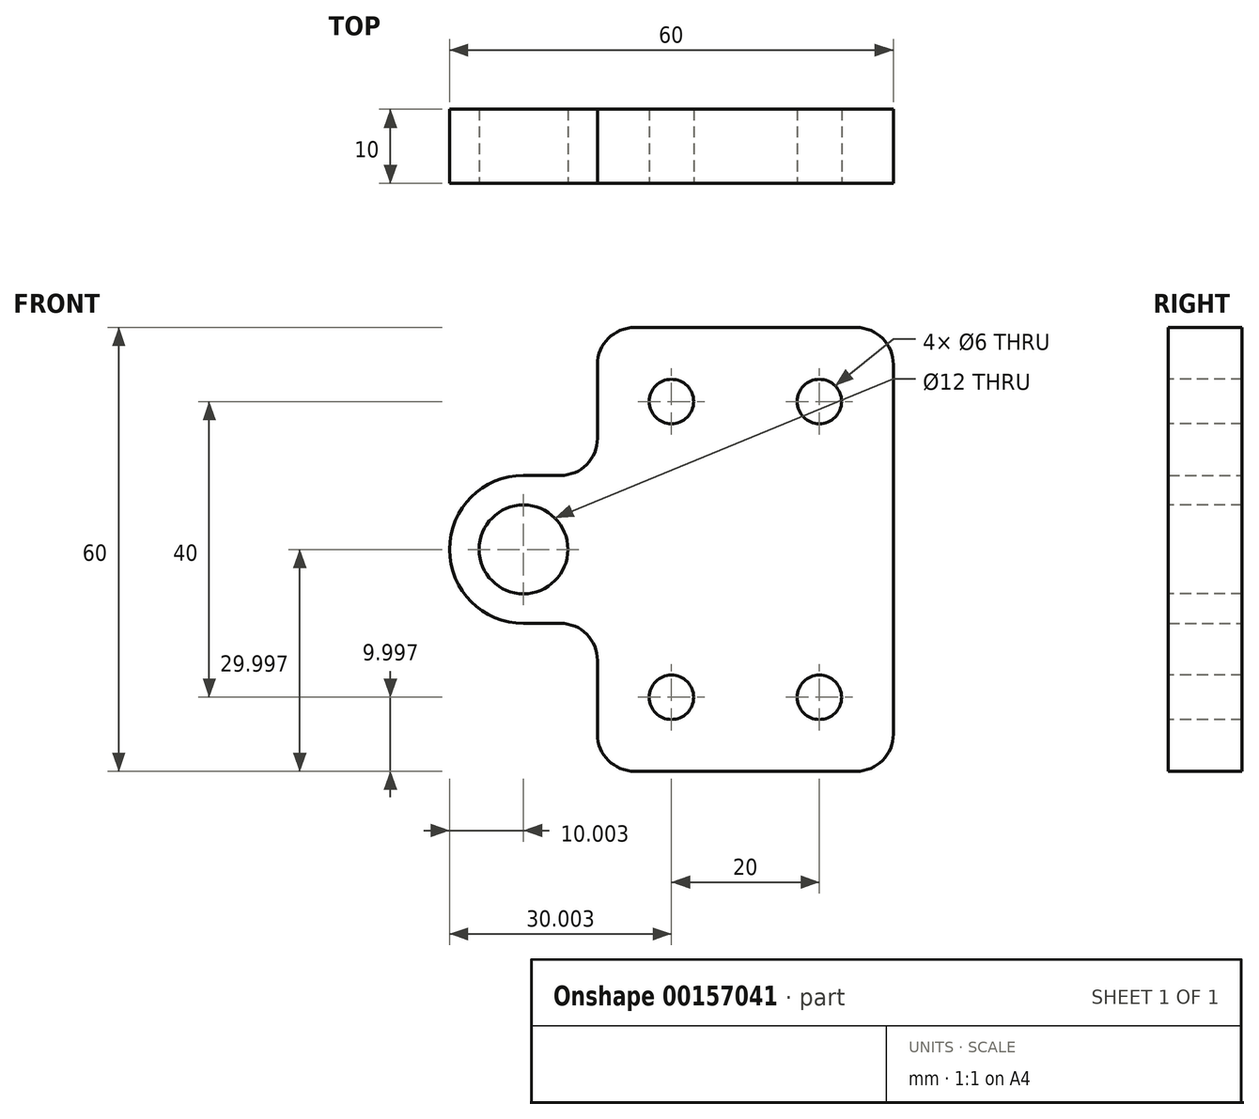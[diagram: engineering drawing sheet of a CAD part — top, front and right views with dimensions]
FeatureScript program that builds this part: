
annotation { "Feature Type Name" : "Feature", "Feature Type Description" : "" }
export const myFeature = defineFeature(function(context is Context, id is Id, definition is map)
    precondition{}
    {
        {
            var Q0;
            Q0=qCreatedBy(makeId("Front.planeOp"),FACE);
            var sketch = newSketch(context, id + "F0", { "sketchPlane" : qUnion([Q0])});
            skLineSegment(sketch, "E0.bottom", {"start": v(-14.72, -1.01) * mm, "end": v(-54.72, -1.01) * mm});
            skLineSegment(sketch, "E0.top", {"start": v(-14.72, 58.99) * mm, "end": v(-54.72, 58.99) * mm});
            skLineSegment(sketch, "E0.left", {"start": v(-14.72, -1.01) * mm, "end": v(-14.72, 58.99) * mm});
            skLineSegment(sketch, "E0.right", {"start": v(-54.72, -1.01) * mm, "end": v(-54.72, 58.99) * mm});
            skLineSegment(sketch, "E1.bottom", {"start": v(-54.72, 18.99) * mm, "end": v(-74.72, 18.99) * mm});
            skLineSegment(sketch, "E1.top", {"start": v(-54.72, 38.99) * mm, "end": v(-74.72, 38.99) * mm});
            skLineSegment(sketch, "E1.left", {"start": v(-54.72, 18.99) * mm, "end": v(-54.72, 38.99) * mm});
            skLineSegment(sketch, "E1.right", {"start": v(-74.72, 18.99) * mm, "end": v(-74.72, 38.99) * mm});
            skSolve(sketch);
        }
        {
            var Q0;
            {var subQ1=sQuery(id+"F0.wireOp",EDGE,"E0.bottom");Q0=makeQuery(id+"F0.imprint","IMPRINT",FACE,{"disambiguationData":[TD([[makeQuery(id+"F0.imprint","IMPRINT",EDGE,{"derivedFrom":subQ1}),-1.0]])]});}
            var Q1;
            Q1=makeQuery(id+"F0.imprint","IMPRINT",FACE,{"disambiguationData":[TD([[makeQuery(id+"F0.imprint","IMPRINT",EDGE,{"derivedFrom":sQuery(id+"F0.wireOp",EDGE,"E1.bottom")}),-1.0]])]});
            extrude(context, id + "F1", {"entities" : qUnion([Q0, Q1]), "depth" : 10 * mm});
        }
        {
            var Q0;
            Q0=makeQuery(id+"F1.opExtrude","SWEPT_EDGE",EDGE,{"disambiguationData":[OSD([sQuery(id+"F0.wireOp",EDGE,"E0.top"),sQuery(id+"F0.wireOp",EDGE,"E0.right")])]});
            var Q1;
            Q1=makeQuery(id+"F1.opExtrude","SWEPT_EDGE",EDGE,{"disambiguationData":[OSD([sQuery(id+"F0.wireOp",EDGE,"E0.bottom"),sQuery(id+"F0.wireOp",EDGE,"E0.right")])]});
            var Q2;
            Q2=makeQuery(id+"F1.opExtrude","SWEPT_EDGE",EDGE,{"disambiguationData":[OSD([sQuery(id+"F0.wireOp",EDGE,"E0.top"),sQuery(id+"F0.wireOp",EDGE,"E0.left")])]});
            var Q3;
            Q3=makeQuery(id+"F1.opExtrude","SWEPT_EDGE",EDGE,{"disambiguationData":[OSD([sQuery(id+"F0.wireOp",EDGE,"E0.bottom"),sQuery(id+"F0.wireOp",EDGE,"E0.left")])]});
            var Q4;
            Q4=makeQuery(id+"F1.opExtrude","SWEPT_EDGE",EDGE,{"disambiguationData":[OSD([sQuery(id+"F0.wireOp",EDGE,"E0.right"),sQuery(id+"F0.wireOp",EDGE,"E1.bottom"),sQuery(id+"F0.wireOp",EDGE,"E1.left")])]});
            var Q5;
            Q5=makeQuery(id+"F1.opExtrude","SWEPT_EDGE",EDGE,{"disambiguationData":[OSD([sQuery(id+"F0.wireOp",EDGE,"E0.right"),sQuery(id+"F0.wireOp",EDGE,"E1.top"),sQuery(id+"F0.wireOp",EDGE,"E1.left")])]});
            fillet(context, id + "F2", {"entities" : qUnion([Q0, Q1, Q2, Q3, Q4, Q5]), "radius" : 5 * mm, "tangentPropagation" : true, "allowEdgeOverflow" : false});
        }
        {
            var Q0;
            Q0=makeQuery(id+"F1.opExtrude","SWEPT_EDGE",EDGE,{"disambiguationData":[OSD([sQuery(id+"F0.wireOp",EDGE,"E1.top"),sQuery(id+"F0.wireOp",EDGE,"E1.right")])]});
            var Q1;
            Q1=makeQuery(id+"F1.opExtrude","SWEPT_EDGE",EDGE,{"disambiguationData":[OSD([sQuery(id+"F0.wireOp",EDGE,"E1.bottom"),sQuery(id+"F0.wireOp",EDGE,"E1.right")])]});
            fillet(context, id + "F3", {"entities" : qUnion([Q0, Q1]), "radius" : 10 * mm, "tangentPropagation" : true, "allowEdgeOverflow" : false});
        }
        {
            var Q0;
            Q0=makeQuery(id+"F1.opExtrude","CAP_FACE",FACE,{"disambiguationData":[OSD([sQuery(id+"F0.wireOp",EDGE,"E0.bottom"),sQuery(id+"F0.wireOp",EDGE,"E0.top"),sQuery(id+"F0.wireOp",EDGE,"E0.left"),sQuery(id+"F0.wireOp",EDGE,"E0.right"),sQuery(id+"F0.wireOp",EDGE,"E1.bottom"),sQuery(id+"F0.wireOp",EDGE,"E1.top"),sQuery(id+"F0.wireOp",EDGE,"E1.right")])],"isStart":false});
            var sketch = newSketch(context, id + "F4", { "sketchPlane" : qUnion([Q0])});
            skPoint(sketch, "E2", {"position": v(-44.72, 48.99) * mm});
            skPoint(sketch, "E3", {"position": v(-24.72, 48.99) * mm});
            skLineSegment(sketch, "E4", {"start": v(-74.72, 28.99) * mm, "end": v(-14.72, 28.99) * mm});
            skPoint(sketch, "E5.MirrorP", {"position": v(-44.72, 8.99) * mm});
            skPoint(sketch, "E6.MirrorP", {"position": v(-24.72, 8.99) * mm});
            skSolve(sketch);
        }
        {
            var Q0;
            Q0=sQuery(id+"F4.wireOp",VERTEX,"E2");
            var Q1;
            Q1=sQuery(id+"F4.wireOp",VERTEX,"E3");
            var Q2;
            Q2=sQuery(id+"F4.wireOp",VERTEX,"E6.MirrorP");
            var Q3;
            Q3=sQuery(id+"F4.wireOp",VERTEX,"E5.MirrorP");
            var Q4;
            Q4=makeQuery(id+"F1.opExtrude","SWEPT_BODY",BODY,{"disambiguationData":[OSD([sQuery(id+"F0.wireOp",EDGE,"E0.bottom"),sQuery(id+"F0.wireOp",EDGE,"E0.top"),sQuery(id+"F0.wireOp",EDGE,"E0.left"),sQuery(id+"F0.wireOp",EDGE,"E0.right"),sQuery(id+"F0.wireOp",EDGE,"E1.bottom"),sQuery(id+"F0.wireOp",EDGE,"E1.top"),sQuery(id+"F0.wireOp",EDGE,"E1.right")])]});
            hole(context, id + "F5", {"style" : HoleStyle.SIMPLE, "endStyle" : HoleEndStyle.THROUGH, "holeDiameter" : 6 * mm, "locations" : qUnion([Q0, Q1, Q2, Q3]), "scope" : qUnion([Q4]), "isTappedThrough" : true});
        }
        {
            var Q0;
            Q0=makeQuery(id+"F1.opExtrude","CAP_FACE",FACE,{"disambiguationData":[OSD([sQuery(id+"F0.wireOp",EDGE,"E0.bottom"),sQuery(id+"F0.wireOp",EDGE,"E0.top"),sQuery(id+"F0.wireOp",EDGE,"E0.left"),sQuery(id+"F0.wireOp",EDGE,"E0.right"),sQuery(id+"F0.wireOp",EDGE,"E1.bottom"),sQuery(id+"F0.wireOp",EDGE,"E1.top"),sQuery(id+"F0.wireOp",EDGE,"E1.right")])],"isStart":false});
            var sketch = newSketch(context, id + "F6", { "sketchPlane" : qUnion([Q0])});
            skPoint(sketch, "E7", {"position": v(-64.72, 28.99) * mm});
            skSolve(sketch);
        }
        {
            var Q0;
            Q0=sQuery(id+"F6.wireOp",VERTEX,"E7");
            var Q1;
            Q1=makeQuery(id+"F1.opExtrude","SWEPT_BODY",BODY,{"disambiguationData":[OSD([sQuery(id+"F0.wireOp",EDGE,"E0.bottom"),sQuery(id+"F0.wireOp",EDGE,"E0.top"),sQuery(id+"F0.wireOp",EDGE,"E0.left"),sQuery(id+"F0.wireOp",EDGE,"E0.right"),sQuery(id+"F0.wireOp",EDGE,"E1.bottom"),sQuery(id+"F0.wireOp",EDGE,"E1.top"),sQuery(id+"F0.wireOp",EDGE,"E1.right")])]});
            hole(context, id + "F7", {"style" : HoleStyle.SIMPLE, "endStyle" : HoleEndStyle.THROUGH, "holeDiameter" : 12 * mm, "locations" : qUnion([Q0]), "scope" : qUnion([Q1]), "isTappedThrough" : true});
        }
    });
